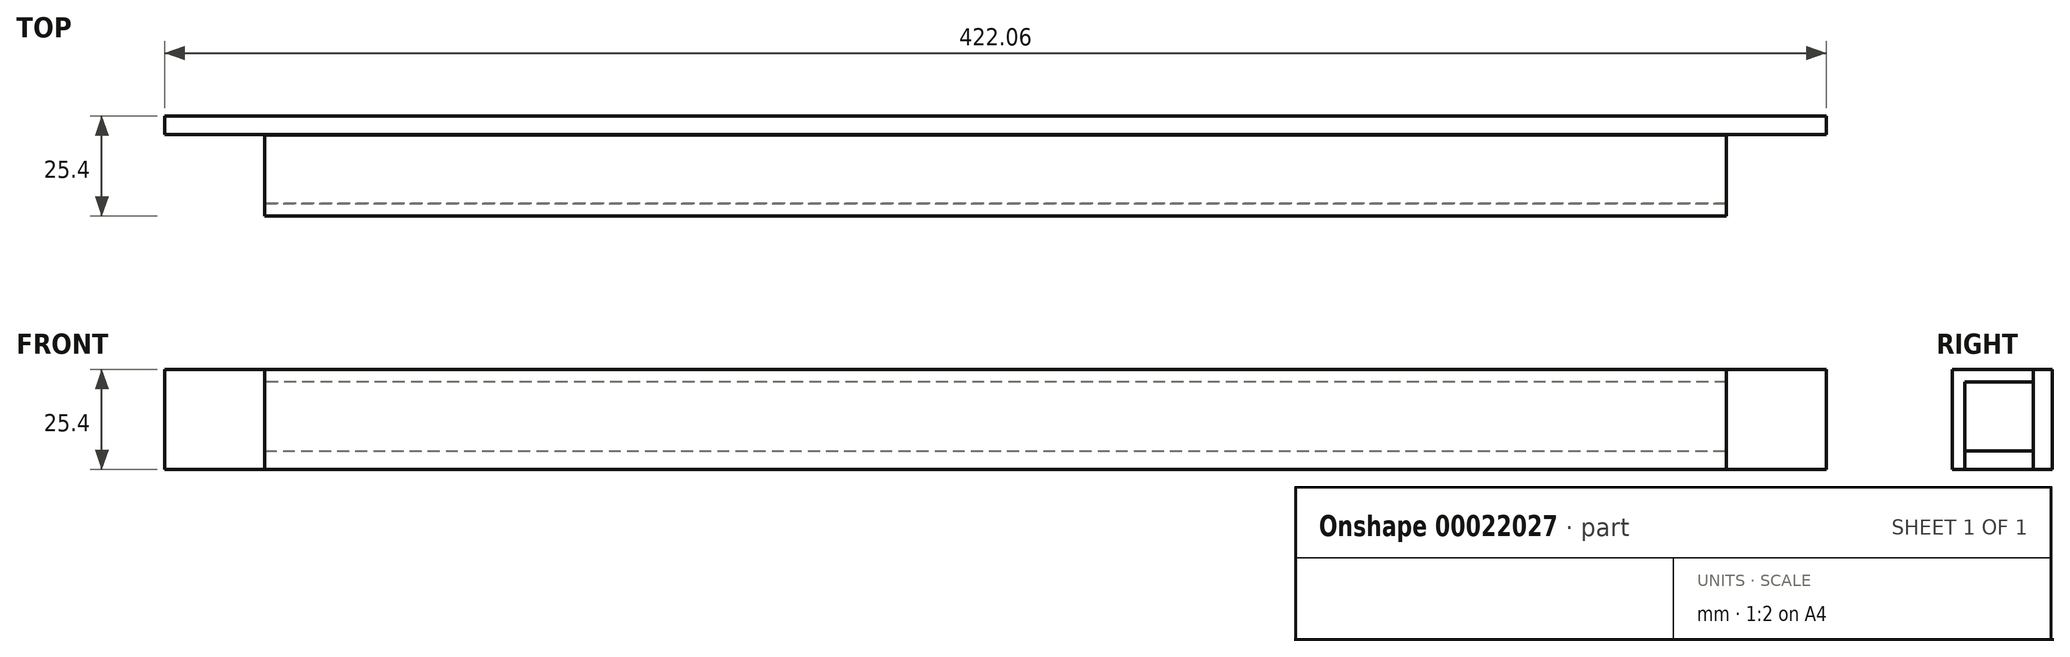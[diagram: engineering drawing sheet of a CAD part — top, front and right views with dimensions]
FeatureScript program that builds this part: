
annotation { "Feature Type Name" : "Feature", "Feature Type Description" : "" }
export const myFeature = defineFeature(function(context is Context, id is Id, definition is map)
    precondition{}
    {
        {
            var Q0;
            Q0=qCreatedBy(makeId("Right.planeOp"),FACE);
            var sketch = newSketch(context, id + "F0", { "sketchPlane" : qUnion([Q0])});
            skLineSegment(sketch, "E0.top", {"start": v(0, -4.76) * mm, "end": v(25.4, -4.76) * mm});
            skLineSegment(sketch, "E0.left", {"start": v(0, 0) * mm, "end": v(0, -4.76) * mm});
            skLineSegment(sketch, "E1.top", {"start": v(25.4, 20.64) * mm, "end": v(20.64, 20.64) * mm});
            skLineSegment(sketch, "E1.left", {"start": v(25.4, -4.76) * mm, "end": v(25.4, 20.64) * mm});
            skLineSegment(sketch, "E1.right", {"start": v(20.64, 0) * mm, "end": v(20.64, 20.64) * mm});
            skLineSegment(sketch, "E2", {"start": v(0, 0) * mm, "end": v(20.64, 0) * mm});
            skSolve(sketch);
        }
        {
            var Q0;
            Q0 = qSketchRegion(id + "F0", true);
            extrude(context, id + "F1", {"entities" : qUnion([Q0]), "depth" : (450 * mm - 27.94 * mm)});
        }
        {
            var Q0;
            Q0=makeQuery(id+"F1.opExtrude","SWEPT_FACE",FACE,{"disambiguationData":[OSD([sQuery(id+"F0.wireOp",EDGE,"E2")])]});
            var sketch = newSketch(context, id + "F2", { "sketchPlane" : qUnion([Q0])});
            skLineSegment(sketch, "E3.bottom", {"start": v(422.06, 20.64) * mm, "end": v(396.66, 20.64) * mm});
            skLineSegment(sketch, "E3.top", {"start": v(422.06, 0) * mm, "end": v(396.66, 0) * mm});
            skLineSegment(sketch, "E3.left", {"start": v(422.06, 20.64) * mm, "end": v(422.06, 0) * mm});
            skLineSegment(sketch, "E3.right", {"start": v(396.66, 20.64) * mm, "end": v(396.66, 0) * mm});
            skSolve(sketch);
        }
        {
            var Q0;
            Q0 = qSketchRegion(id + "F2", true);
            extrude(context, id + "F3", {"entities" : qUnion([Q0]), "operationType" : NewBodyOperationType.REMOVE, "oppositeDirection" : true, "depth" : 25.4 * mm});
        }
        {
            var Q0;
            Q0=makeQuery(id+"F1.opExtrude","SWEPT_FACE",FACE,{"disambiguationData":[OSD([sQuery(id+"F0.wireOp",EDGE,"E2")])]});
            var sketch = newSketch(context, id + "F4", { "sketchPlane" : qUnion([Q0])});
            skLineSegment(sketch, "E4.bottom", {"start": v(0, 20.64) * mm, "end": v(25.4, 20.64) * mm});
            skLineSegment(sketch, "E4.top", {"start": v(0, 0) * mm, "end": v(25.4, 0) * mm});
            skLineSegment(sketch, "E4.left", {"start": v(0, 20.64) * mm, "end": v(0, 0) * mm});
            skLineSegment(sketch, "E4.right", {"start": v(25.4, 20.64) * mm, "end": v(25.4, 0) * mm});
            skSolve(sketch);
        }
        {
            var Q0;
            Q0 = qSketchRegion(id + "F4", true);
            extrude(context, id + "F5", {"entities" : qUnion([Q0]), "operationType" : NewBodyOperationType.REMOVE, "oppositeDirection" : true, "depth" : 25.4 * mm});
        }
        {
            var Q0;
            Q0=makeQuery(id+"F5.boolean.opBoolean","COPY",FACE,{"derivedFrom":makeQuery(id+"F5.opExtrude","SWEPT_FACE",FACE,{"disambiguationData":[OSD([sQuery(id+"F4.wireOp",EDGE,"E4.right")])]})});
            var sketch = newSketch(context, id + "F6", { "sketchPlane" : qUnion([Q0])});
            skLineSegment(sketch, "E5", {"start": v(0, -4.76) * mm, "end": v(-3.17, -4.76) * mm});
            skLineSegment(sketch, "E6", {"start": v(-3.17, -4.76) * mm, "end": v(-3.17, 20.64) * mm});
            skLineSegment(sketch, "E7", {"start": v(0, -4.76) * mm, "end": v(0, 20.64) * mm});
            skLineSegment(sketch, "E8", {"start": v(0, 20.64) * mm, "end": v(0, 17.46) * mm});
            skLineSegment(sketch, "E9", {"start": v(0, 17.46) * mm, "end": v(-21.28, 17.46) * mm});
            skLineSegment(sketch, "E10", {"start": v(0, 20.64) * mm, "end": v(-20.62, 20.64) * mm});
            skLineSegment(sketch, "E11", {"start": v(-20.62, 20.64) * mm, "end": v(-21.28, 17.46) * mm});
            skSolve(sketch);
        }
        {
            var Q0;
            Q0 = qSketchRegion(id + "F6", true);
            extrude(context, id + "F7", {"entities" : qUnion([Q0]), "operationType" : NewBodyOperationType.ADD, "oppositeDirection" : true, "depth" : 371.35 * mm});
        }
    });
